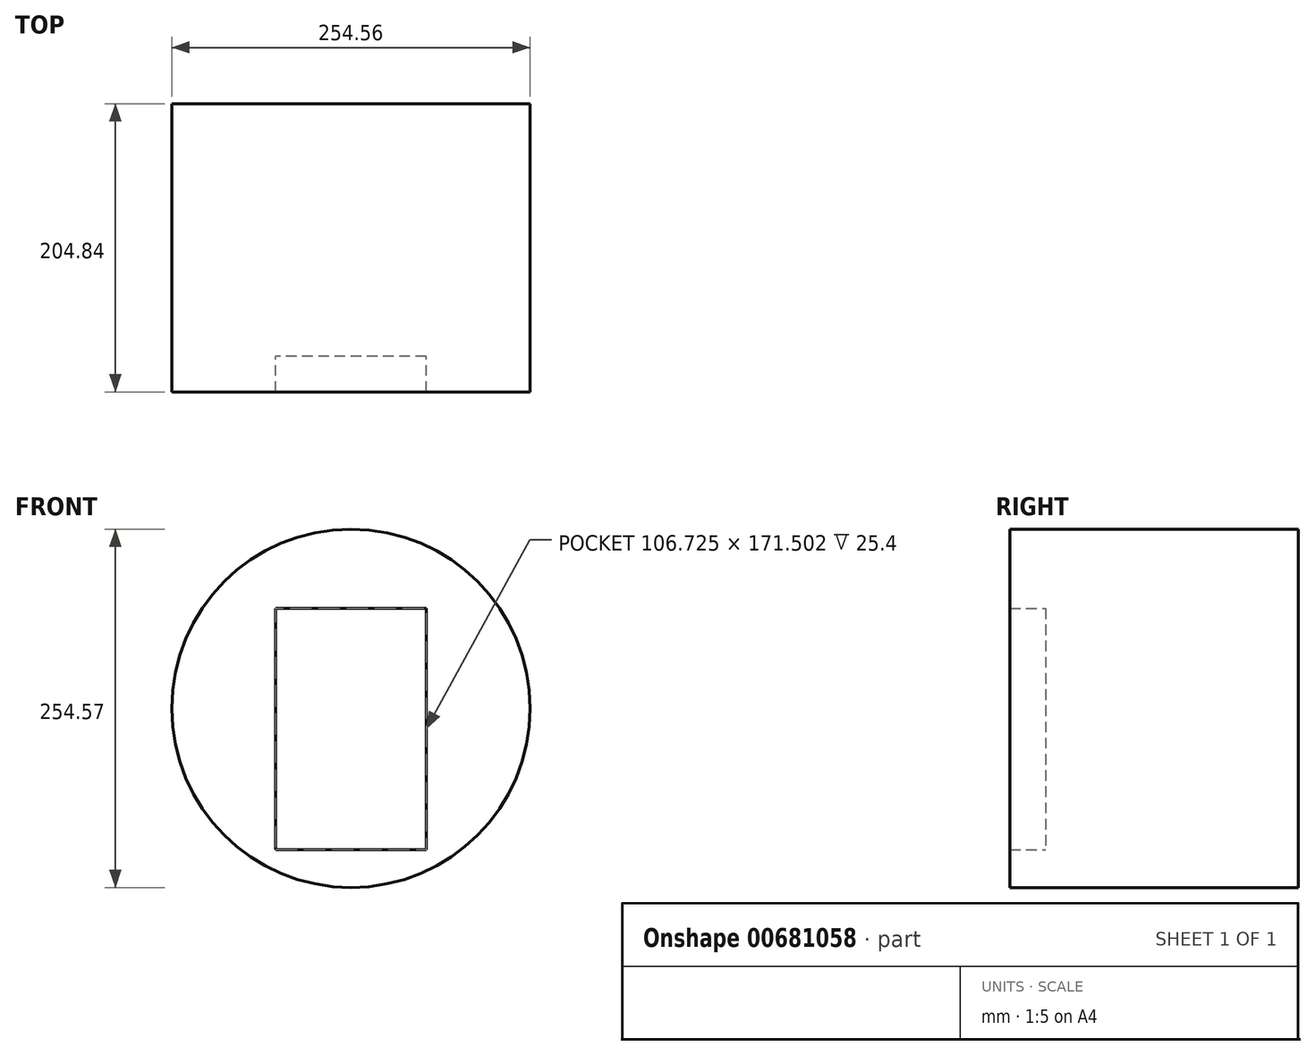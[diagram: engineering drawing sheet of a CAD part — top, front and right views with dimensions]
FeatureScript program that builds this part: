
annotation { "Feature Type Name" : "Feature", "Feature Type Description" : "" }
export const myFeature = defineFeature(function(context is Context, id is Id, definition is map)
    precondition{}
    {
        {
            var Q0;
            Q0=qCreatedBy(makeId("Front.planeOp"),FACE);
            var sketch = newSketch(context, id + "F0", { "sketchPlane" : qUnion([Q0])});
            skCircle(sketch, "E0", {"center": v(0, 14.72) * mm, "radius": 127.28 * mm});
            skSolve(sketch);
        }
        {
            var Q0;
            Q0=makeQuery(id+"F0.imprint","IMPRINT",FACE,{"disambiguationData":[TD([[makeQuery(id+"F0.imprint","IMPRINT",EDGE,{"derivedFrom":sQuery(id+"F0.wireOp",EDGE,"E0")}),1.0]])]});
            extrude(context, id + "F1", {"entities" : qUnion([Q0]), "depth" : 179.44 * mm, "offsetDistance" : 25.4 * mm});
        }
        {
            var Q0;
            Q0=makeQuery(id+"F1.opExtrude","CAP_FACE",FACE,{"disambiguationData":[OSD([sQuery(id+"F0.wireOp",EDGE,"E0")])],"isStart":false});
            var sketch = newSketch(context, id + "F2", { "sketchPlane" : qUnion([Q0])});
            skLineSegment(sketch, "E1.bottom", {"start": v(53.36, 85.75) * mm, "end": v(-53.36, 85.75) * mm});
            skLineSegment(sketch, "E1.top", {"start": v(53.36, -85.75) * mm, "end": v(-53.36, -85.75) * mm});
            skLineSegment(sketch, "E1.left", {"start": v(53.36, 85.75) * mm, "end": v(53.36, -85.75) * mm});
            skLineSegment(sketch, "E1.right", {"start": v(-53.36, 85.75) * mm, "end": v(-53.36, -85.75) * mm});
            skPoint(sketch, "E1.middle", {"position": v(0, 0) * mm});
            skSolve(sketch);
        }
        {
            var Q0;
            Q0=makeQuery(id+"F2.imprint","IMPRINT",FACE,{"disambiguationData":[TD([[makeQuery(id+"F2.imprint","IMPRINT",EDGE,{"derivedFrom":sQuery(id+"F2.wireOp",EDGE,"E1.bottom")}),-1.0]])]});
            extrude(context, id + "F3", {"entities" : qUnion([Q0]), "operationType" : NewBodyOperationType.ADD, "depth" : 25.4 * mm, "offsetDistance" : 25.4 * mm});
        }
    });
